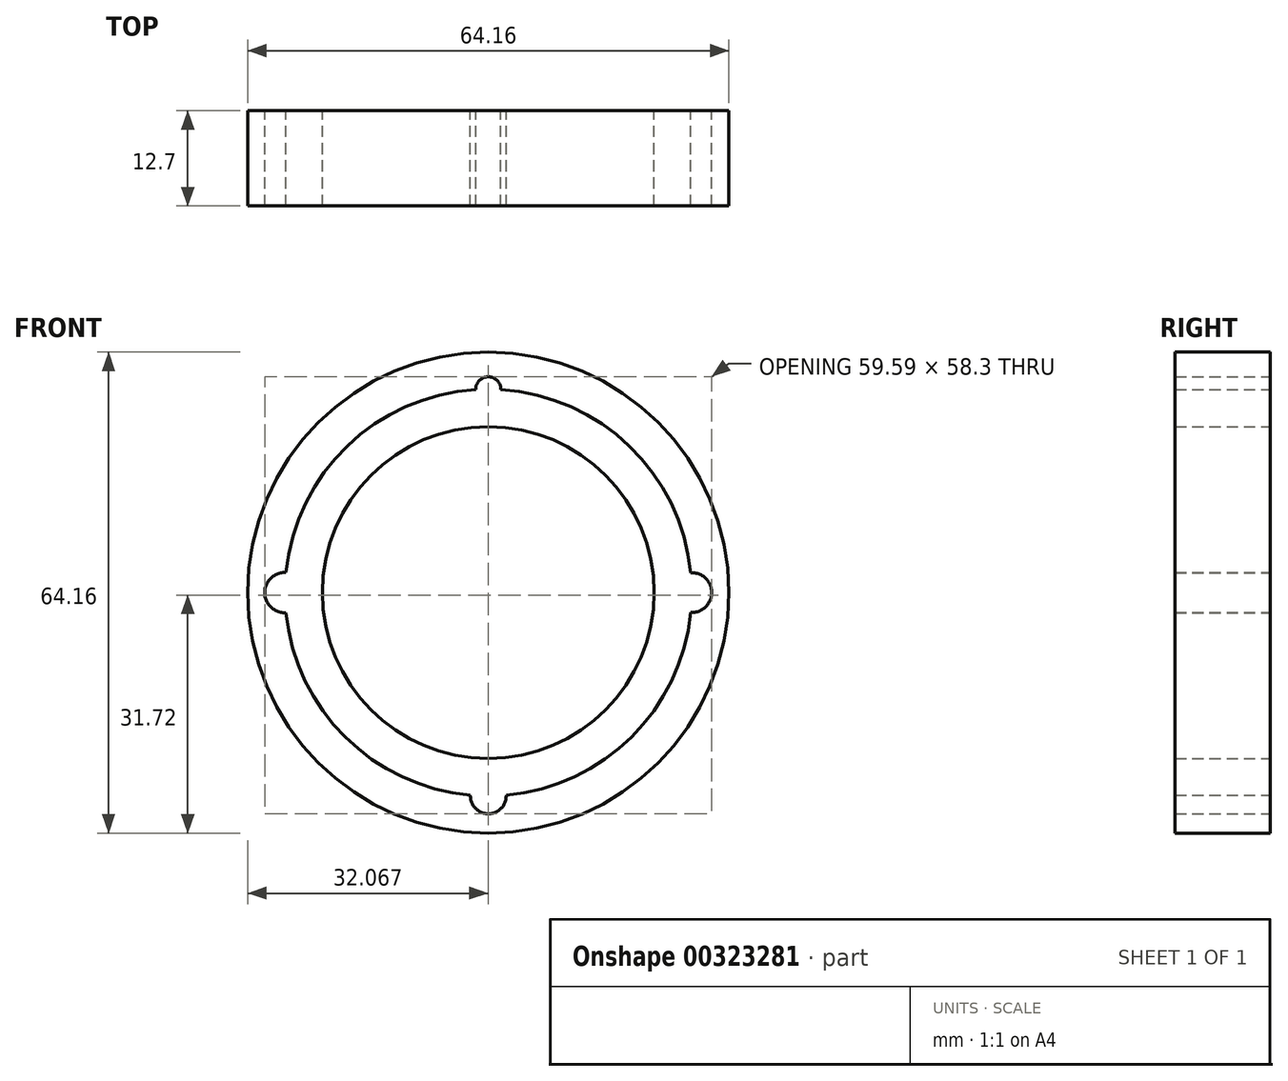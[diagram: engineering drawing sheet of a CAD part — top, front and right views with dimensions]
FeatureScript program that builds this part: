
annotation { "Feature Type Name" : "Feature", "Feature Type Description" : "" }
export const myFeature = defineFeature(function(context is Context, id is Id, definition is map)
    precondition{}
    {
        {
            var Q0;
            Q0=qCreatedBy(makeId("Front.planeOp"),FACE);
            var sketch = newSketch(context, id + "F0", { "sketchPlane" : qUnion([Q0])});
            skCircle(sketch, "E0", {"center": v(0, 0) * mm, "radius": 32.08 * mm});
            skCircle(sketch, "E1", {"center": v(0, 0) * mm, "radius": 22.12 * mm});
            skCircle(sketch, "E2", {"center": v(0, 0) * mm, "radius": 27.12 * mm});
            skCircle(sketch, "E3", {"center": v(0, 27.12) * mm, "radius": 1.67 * mm});
            skCircle(sketch, "E4", {"center": v(0, -27.12) * mm, "radius": 2.4 * mm});
            skCircle(sketch, "E5", {"center": v(27.12, 0) * mm, "radius": 2.66 * mm});
            skCircle(sketch, "E6", {"center": v(-27.12, 0) * mm, "radius": 2.69 * mm});
            skSolve(sketch);
        }
        {
            var Q0;
            Q0 = qSketchRegion(id + "F2", true);
            var Q1;
            Q1=makeQuery(id+"F0.imprint","IMPRINT",FACE,{"disambiguationData":[TD([[makeQuery(id+"F0.imprint","IMPRINT",EDGE,{"derivedFrom":sQuery(id+"F0.wireOp",EDGE,"E0")}),1.0]])]});
            var Q2;
            Q2=makeQuery(id+"F0.imprint","IMPRINT",FACE,{"disambiguationData":[TD([[makeQuery(id+"F0.imprint","IMPRINT",EDGE,{"derivedFrom":sQuery(id+"F0.wireOp",EDGE,"E1")}),1.0]])]});
            extrude(context, id + "F1", {"entities" : qUnion([Q0, Q1, Q2]), "depth" : 12.7 * mm});
        }
        {
            var Q0;
            Q0=qCreatedBy(makeId("Front.planeOp"),FACE);
            var sketch = newSketch(context, id + "F2", { "sketchPlane" : qUnion([Q0])});
            skCircle(sketch, "E7", {"center": v(0, 0) * mm, "radius": 19.44 * mm});
            skSolve(sketch);
        }
        {
            var Q0;
            Q0=sQuery(id+"F2.wireOp",VERTEX,"E7.center");
            var Q1;
            Q1=makeQuery(id+"F1.opExtrude","SWEPT_BODY",BODY,{"disambiguationData":[OSD([sQuery(id+"F0.wireOp",EDGE,"E0")])]});
            hole(context, id + "F3", {"style" : HoleStyle.C_SINK, "endStyle" : HoleEndStyle.THROUGH, "oppositeDirection" : true, "holeDiameter" : 6.35 * mm, "cSinkDiameter" : 12.7 * mm, "cSinkAngle" : 90 * degree, "tappedDepth" : 12.7 * mm, "tapClearance" : 3, "startFromSketch" : true, "locations" : qUnion([Q0]), "scope" : qUnion([Q1])});
        }
    });
